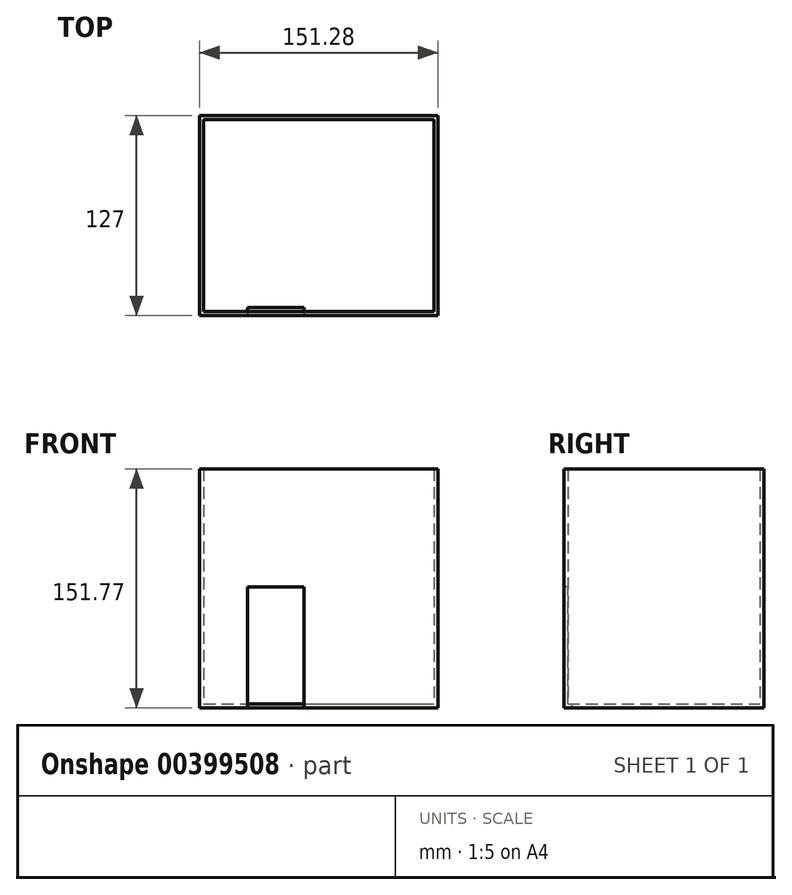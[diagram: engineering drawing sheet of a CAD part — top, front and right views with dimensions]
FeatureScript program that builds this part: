
annotation { "Feature Type Name" : "Feature", "Feature Type Description" : "" }
export const myFeature = defineFeature(function(context is Context, id is Id, definition is map)
    precondition{}
    {
        {
            var Q0;
            Q0=qCreatedBy(makeId("Top.planeOp"),FACE);
            var sketch = newSketch(context, id + "F0", { "sketchPlane" : qUnion([Q0])});
            skLineSegment(sketch, "E0.bottom", {"start": v(-76.76, -75.18) * mm, "end": v(75.51, -75.18) * mm});
            skLineSegment(sketch, "E0.top", {"start": v(-76.76, 76) * mm, "end": v(75.51, 76) * mm});
            skLineSegment(sketch, "E0.left", {"start": v(-76.76, -75.18) * mm, "end": v(-76.76, 76) * mm});
            skLineSegment(sketch, "E0.right", {"start": v(75.51, -75.18) * mm, "end": v(75.51, 76) * mm});
            skSolve(sketch);
        }
        {
            var Q0;
            Q0=makeQuery(id+"F0.imprint","IMPRINT",FACE,{"disambiguationData":[TD([[makeQuery(id+"F0.imprint","IMPRINT",EDGE,{"derivedFrom":sQuery(id+"F0.wireOp",EDGE,"E0.bottom")}),1.0]])]});
            extrude(context, id + "F1", {"entities" : qUnion([Q0]), "depth" : 101.6 * mm});
        }
        {
            var Q0;
            Q0=makeQuery(id+"F1.opExtrude","CAP_FACE",FACE,{"disambiguationData":[OSD([sQuery(id+"F0.wireOp",EDGE,"E0.bottom"),sQuery(id+"F0.wireOp",EDGE,"E0.top"),sQuery(id+"F0.wireOp",EDGE,"E0.left"),sQuery(id+"F0.wireOp",EDGE,"E0.right")])],"isStart":false});
            chamfer(context, id + "F2", {"entities" : qUnion([Q0]), "width" : 50.8 * mm, "tangentPropagation" : true});
        }
        {
            var Q0;
            Q0=makeQuery(id+"F1.opExtrude","CAP_EDGE",EDGE,{"disambiguationData":[OSD([sQuery(id+"F0.wireOp",EDGE,"E0.bottom")])],"isStart":true});
            chamfer(context, id + "F3", {"entities" : qUnion([Q0]), "width" : 50.8 * mm, "tangentPropagation" : true});
        }
        {
            var Q0;
            Q0=makeQuery(id+"F1.opExtrude","SWEPT_EDGE",EDGE,{"disambiguationData":[OSD([sQuery(id+"F0.wireOp",EDGE,"E0.top"),sQuery(id+"F0.wireOp",EDGE,"E0.right")])]});
            chamfer(context, id + "F4", {"entities" : qUnion([Q0]), "width" : 50.8 * mm, "tangentPropagation" : true});
        }
        {
            var Q0;
            Q0=makeQuery(id+"F1.opExtrude","CAP_FACE",FACE,{"disambiguationData":[OSD([sQuery(id+"F0.wireOp",EDGE,"E0.bottom"),sQuery(id+"F0.wireOp",EDGE,"E0.top"),sQuery(id+"F0.wireOp",EDGE,"E0.left"),sQuery(id+"F0.wireOp",EDGE,"E0.right")])],"isStart":false});
            shell(context, id + "F5", {"entities" : qUnion([Q0]), "thickness" : 2.54 * mm});
        }
        {
            var Q0;
            Q0=makeQuery(id+"F1.opExtrude","SWEPT_BODY",BODY,{"disambiguationData":[OSD([sQuery(id+"F0.wireOp",EDGE,"E0.bottom"),sQuery(id+"F0.wireOp",EDGE,"E0.top"),sQuery(id+"F0.wireOp",EDGE,"E0.left"),sQuery(id+"F0.wireOp",EDGE,"E0.right")])]});
            deleteBodies(context, id + "F6", {"entities" : qUnion([Q0])});
        }
        {
            var Q0;
            Q0=qCreatedBy(makeId("Front.planeOp"),FACE);
            var sketch = newSketch(context, id + "F7", { "sketchPlane" : qUnion([Q0])});
            skLineSegment(sketch, "E1.bottom", {"start": v(-76.01, 74.9) * mm, "end": v(75.27, 74.9) * mm});
            skLineSegment(sketch, "E1.top", {"start": v(-76.01, -76.88) * mm, "end": v(75.27, -76.88) * mm});
            skLineSegment(sketch, "E1.left", {"start": v(-76.01, 74.9) * mm, "end": v(-76.01, -76.88) * mm});
            skLineSegment(sketch, "E1.right", {"start": v(75.27, 74.9) * mm, "end": v(75.27, -76.88) * mm});
            skSolve(sketch);
        }
        {
            var Q0;
            Q0=makeQuery(id+"F7.imprint","IMPRINT",FACE,{"disambiguationData":[TD([[makeQuery(id+"F7.imprint","IMPRINT",EDGE,{"derivedFrom":sQuery(id+"F7.wireOp",EDGE,"E1.bottom")}),-1.0]])]});
            extrude(context, id + "F8", {"entities" : qUnion([Q0]), "depth" : 127 * mm});
        }
        {
            var Q0;
            Q0=makeQuery(id+"F8.opExtrude","SWEPT_FACE",FACE,{"disambiguationData":[OSD([sQuery(id+"F7.wireOp",EDGE,"E1.bottom")])]});
            shell(context, id + "F9", {"entities" : qUnion([Q0]), "thickness" : 2.54 * mm});
        }
        {
            var Q0;
            Q0=makeQuery(id+"F8.opExtrude","CAP_FACE",FACE,{"disambiguationData":[OSD([sQuery(id+"F7.wireOp",EDGE,"E1.bottom"),sQuery(id+"F7.wireOp",EDGE,"E1.top"),sQuery(id+"F7.wireOp",EDGE,"E1.left"),sQuery(id+"F7.wireOp",EDGE,"E1.right")])],"isStart":false});
            var sketch = newSketch(context, id + "F10", { "sketchPlane" : qUnion([Q0])});
            skLineSegment(sketch, "E2.bottom", {"start": v(-45.54, -76.88) * mm, "end": v(-9.89, -76.88) * mm});
            skLineSegment(sketch, "E2.top", {"start": v(-45.54, 0) * mm, "end": v(-9.89, 0) * mm});
            skLineSegment(sketch, "E2.left", {"start": v(-45.54, -76.88) * mm, "end": v(-45.54, 0) * mm});
            skLineSegment(sketch, "E2.right", {"start": v(-9.89, -76.88) * mm, "end": v(-9.89, 0) * mm});
            skSolve(sketch);
        }
        {
            var Q0;
            Q0=makeQuery(id+"F10.imprint","IMPRINT",FACE,{"disambiguationData":[TD([[makeQuery(id+"F10.imprint","IMPRINT",EDGE,{"derivedFrom":sQuery(id+"F10.wireOp",EDGE,"E2.bottom")}),1.0]])]});
            extrude(context, id + "F11", {"entities" : qUnion([Q0]), "operationType" : NewBodyOperationType.ADD, "depth" : 0.03 * mm});
        }
        {
            var Q0;
            Q0=makeQuery(id+"F11.opExtrude","CAP_FACE",FACE,{"disambiguationData":[OSD([sQuery(id+"F10.wireOp",EDGE,"E2.bottom"),sQuery(id+"F10.wireOp",EDGE,"E2.top"),sQuery(id+"F10.wireOp",EDGE,"E2.left"),sQuery(id+"F10.wireOp",EDGE,"E2.right")])],"isStart":false});
            extrude(context, id + "F12", {"entities" : qUnion([Q0]), "operationType" : NewBodyOperationType.REMOVE, "oppositeDirection" : true, "depth" : 2.54 * mm});
        }
        {
            var Q0;
            Q0=makeQuery(id+"F12.boolean.opBoolean","COPY",FACE,{"derivedFrom":makeQuery(id+"F12.opExtrude","CAP_FACE",FACE,{"disambiguationData":[OSD([sQuery(id+"F10.wireOp",EDGE,"E2.bottom"),sQuery(id+"F10.wireOp",EDGE,"E2.top"),sQuery(id+"F10.wireOp",EDGE,"E2.left"),sQuery(id+"F10.wireOp",EDGE,"E2.right")])],"isStart":false})});
            extrude(context, id + "F13", {"entities" : qUnion([Q0]), "operationType" : NewBodyOperationType.REMOVE, "oppositeDirection" : true, "depth" : 2.54 * mm});
        }
    });
